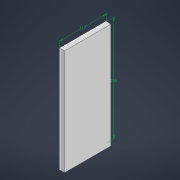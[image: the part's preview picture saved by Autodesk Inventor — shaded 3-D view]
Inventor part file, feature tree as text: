
AUTODESK INVENTOR PART (.ipt)
format: ipt  version: 2022 (Build 260153000, 153)  size: 87,552 bytes
history: native  units: mm
features: other x1, sketch x1, extrude x1
ambient origin geometry x8: Origin, YZ Plane, XZ Plane, XY Plane, X Axis, Y Axis, Z Axis, Center Point
bodies: Body1 (feature_tree)
feature tree (3):
  other  "Твердое тело1"
  sketch  "Эскиз1"
  extrude  "Выдавливание1"  Depth=266.0mm
